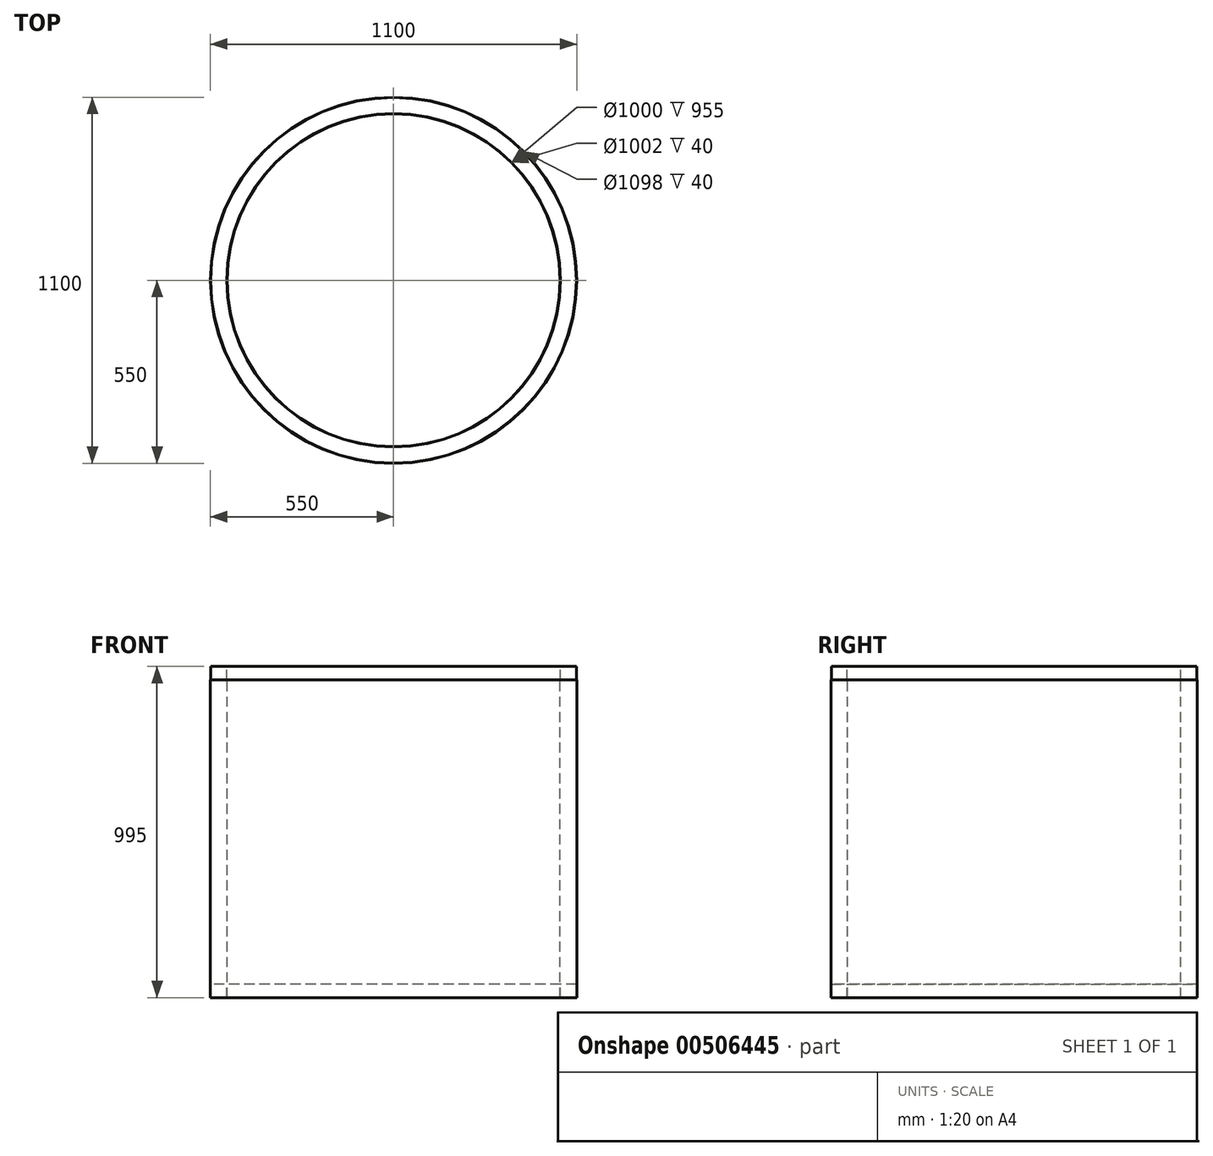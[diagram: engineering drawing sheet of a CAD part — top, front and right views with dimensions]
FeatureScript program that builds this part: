
annotation { "Feature Type Name" : "Feature", "Feature Type Description" : "" }
export const myFeature = defineFeature(function(context is Context, id is Id, definition is map)
    precondition{}
    {
        {
            var Q0;
            Q0=qCreatedBy(makeId("Front.planeOp"),FACE);
            var sketch = newSketch(context, id + "F0", { "sketchPlane" : qUnion([Q0])});
            skLineSegment(sketch, "E0", {"start": v(0, 452.89) * mm, "end": v(0, -450.9) * mm, "construction": true});
            skLineSegment(sketch, "E1", {"start": v(-500, -411.7) * mm, "end": v(-500, 543.3) * mm});
            skLineSegment(sketch, "E2", {"start": v(-500, 543.3) * mm, "end": v(-501, 543.3) * mm});
            skLineSegment(sketch, "E3", {"start": v(-501, 543.3) * mm, "end": v(-501, 583.3) * mm});
            skLineSegment(sketch, "E4", {"start": v(-501, 583.3) * mm, "end": v(-549, 583.3) * mm});
            skLineSegment(sketch, "E5", {"start": v(-549, 583.3) * mm, "end": v(-549, 543.3) * mm});
            skLineSegment(sketch, "E6", {"start": v(-549, 543.3) * mm, "end": v(-550, 543.3) * mm});
            skLineSegment(sketch, "E7", {"start": v(-550, 543.3) * mm, "end": v(-550, -411.7) * mm});
            skLineSegment(sketch, "E8", {"start": v(-550, -411.7) * mm, "end": v(-549, -411.7) * mm});
            skLineSegment(sketch, "E9", {"start": v(-549, -411.7) * mm, "end": v(-549, -371.7) * mm});
            skLineSegment(sketch, "E10", {"start": v(-549, -371.7) * mm, "end": v(-501, -371.7) * mm});
            skLineSegment(sketch, "E11", {"start": v(-501, -371.7) * mm, "end": v(-501, -411.7) * mm});
            skLineSegment(sketch, "E12", {"start": v(-501, -411.7) * mm, "end": v(-500, -411.7) * mm});
            skSolve(sketch);
        }
        {
            var Q0;
            Q0=qSketchRegion(id+"F0",true);
            var Q1;
            Q1=sQuery(id+"F0.wireOp",EDGE,"E0");
            revolve(context, id + "F1", {"entities" : qUnion([Q0]), "axis" : qUnion([Q1]), "revolveType" : RevolveType.FULL});
        }
    });
